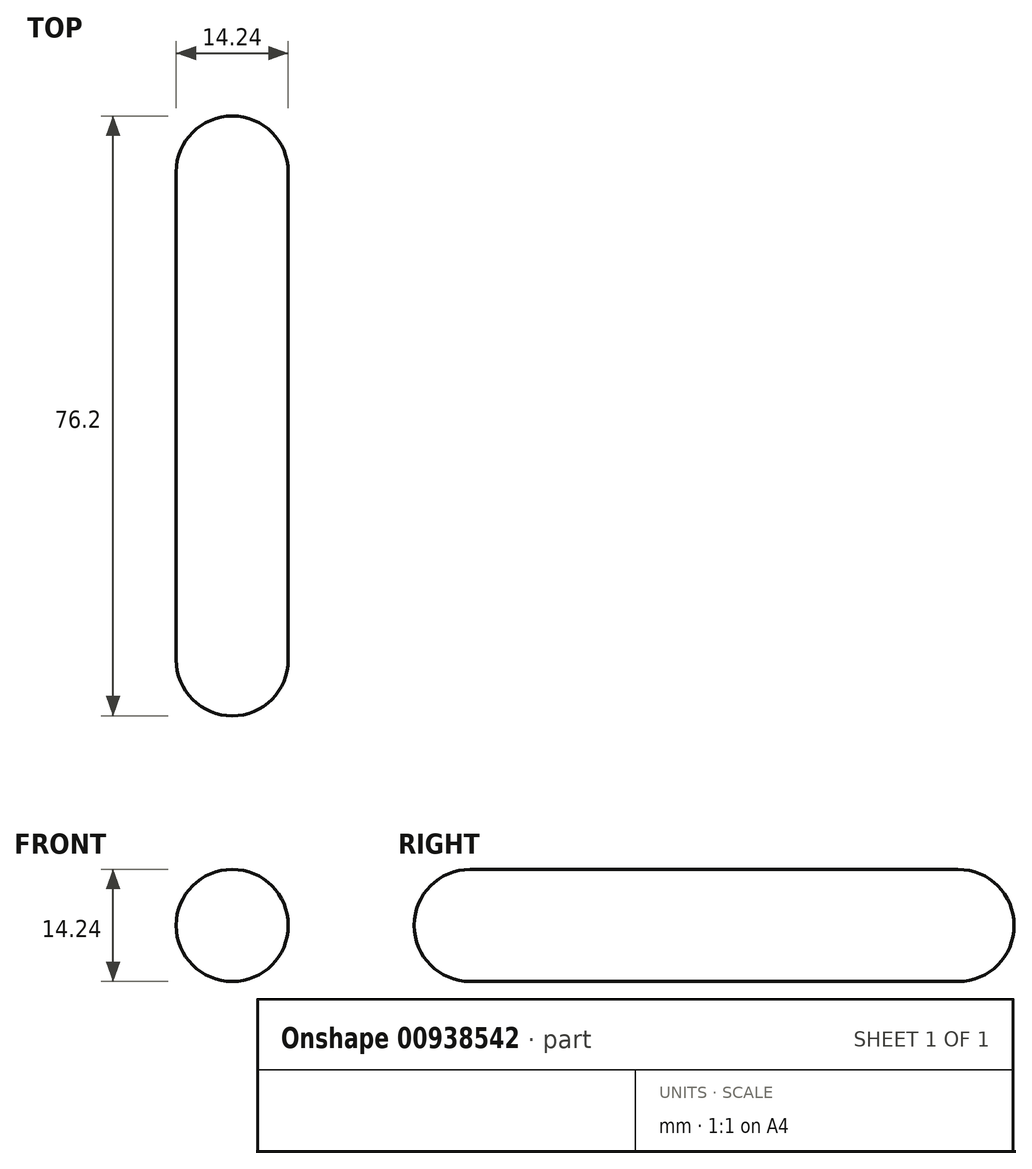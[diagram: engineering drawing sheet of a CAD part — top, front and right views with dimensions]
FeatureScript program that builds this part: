
annotation { "Feature Type Name" : "Feature", "Feature Type Description" : "" }
export const myFeature = defineFeature(function(context is Context, id is Id, definition is map)
    precondition{}
    {
        {
            var Q0;
            Q0=qCreatedBy(makeId("Top.planeOp"),FACE);
            var sketch = newSketch(context, id + "F0", { "sketchPlane" : qUnion([Q0])});
            skLineSegment(sketch, "E0.bottom", {"start": v(-7.12, 38.1) * mm, "end": v(7.12, 38.1) * mm});
            skLineSegment(sketch, "E0.top", {"start": v(-7.12, -38.1) * mm, "end": v(7.12, -38.1) * mm});
            skLineSegment(sketch, "E0.left", {"start": v(-7.12, 38.1) * mm, "end": v(-7.12, -38.1) * mm});
            skLineSegment(sketch, "E0.right", {"start": v(7.12, 38.1) * mm, "end": v(7.12, -38.1) * mm});
            skPoint(sketch, "E0.middle", {"position": v(0, 0) * mm});
            skSolve(sketch);
        }
        {
            var Q0;
            Q0=makeQuery(id+"F0.imprint","IMPRINT",FACE,{"disambiguationData":[TD([[makeQuery(id+"F0.imprint","IMPRINT",EDGE,{"derivedFrom":sQuery(id+"F0.wireOp",EDGE,"E0.bottom")}),-1.0]])]});
            extrude(context, id + "F1", {"entities" : qUnion([Q0]), "depth" : 14.24 * mm, "offsetDistance" : 25 * mm});
        }
        {
            var Q0;
            Q0=makeQuery(id+"F1.opExtrude","CAP_FACE",FACE,{"disambiguationData":[OSD([sQuery(id+"F0.wireOp",EDGE,"E0.bottom"),sQuery(id+"F0.wireOp",EDGE,"E0.top"),sQuery(id+"F0.wireOp",EDGE,"E0.left"),sQuery(id+"F0.wireOp",EDGE,"E0.right")])],"isStart":true});
            var Q1;
            Q1=makeQuery(id+"F1.opExtrude","SWEPT_FACE",FACE,{"disambiguationData":[OSD([sQuery(id+"F0.wireOp",EDGE,"E0.right")])]});
            var Q2;
            Q2=makeQuery(id+"F1.opExtrude","CAP_FACE",FACE,{"disambiguationData":[OSD([sQuery(id+"F0.wireOp",EDGE,"E0.bottom"),sQuery(id+"F0.wireOp",EDGE,"E0.top"),sQuery(id+"F0.wireOp",EDGE,"E0.left"),sQuery(id+"F0.wireOp",EDGE,"E0.right")])],"isStart":false});
            var Q3;
            Q3=makeQuery(id+"F1.opExtrude","SWEPT_FACE",FACE,{"disambiguationData":[OSD([sQuery(id+"F0.wireOp",EDGE,"E0.left")])]});
            fillet(context, id + "F2", {"entities" : qUnion([Q0, Q1, Q2, Q3]), "radius" : 7.11 * mm, "tangentPropagation" : true, "allowEdgeOverflow" : false});
        }
    });
